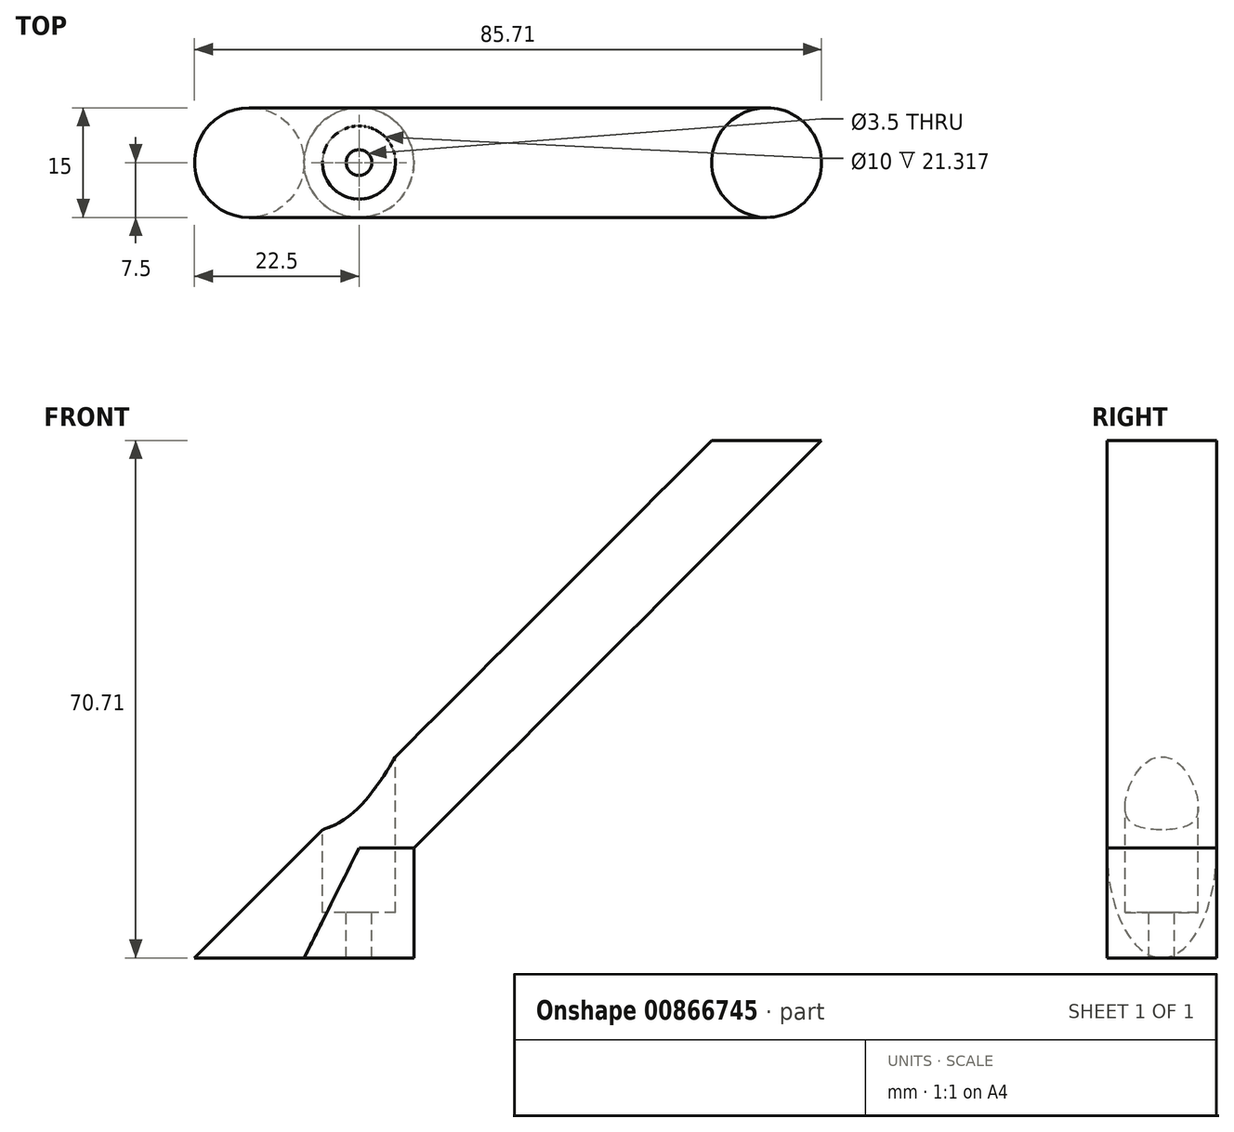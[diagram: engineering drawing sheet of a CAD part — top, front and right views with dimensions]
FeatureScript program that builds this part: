
annotation { "Feature Type Name" : "Feature", "Feature Type Description" : "" }
export const myFeature = defineFeature(function(context is Context, id is Id, definition is map)
    precondition{}
    {
        {
            assignVariable(context, id + "F0", {"variableType" : VariableType.LENGTH, "name" : "InsertWidth", "lengthValue" : 3.5 * mm});
        }
        {
            assignVariable(context, id + "F1", {"variableType" : VariableType.LENGTH, "name" : "LegBaseDepth", "lengthValue" : 15 * mm});
        }
        {
            var Q0;
            Q0=qCreatedBy(makeId("Top.planeOp"),FACE);
            var sketch = newSketch(context, id + "F2", { "sketchPlane" : qUnion([Q0])});
            skCircle(sketch, "E0", {"center": v(0, 0) * mm, "radius": 7.5 * mm});
            skCircle(sketch, "E1", {"center": v(0, 0) * mm, "radius": 1.75 * mm});
            skSolve(sketch);
        }
        {
            var Q0;
            Q0 = qSketchRegion(id + "F2", true);
            var Q1;
            Q1=makeQuery(id+"F2.imprint","IMPRINT",FACE,{"disambiguationData":[TD([[makeQuery(id+"F2.imprint","IMPRINT",EDGE,{"derivedFrom":sQuery(id+"F2.wireOp",EDGE,"E1")}),1.0]])]});
            extrude(context, id + "F3", {"entities" : qUnion([Q0, Q1]), "depth" : getVariable(context, 'LegBaseDepth'), "offsetDistance" : 25 * mm});
        }
        {
            var Q0;
            Q0=qCreatedBy(makeId("Front.planeOp"),FACE);
            var sketch = newSketch(context, id + "F4", { "sketchPlane" : qUnion([Q0])});
            skLineSegment(sketch, "E2", {"start": v(0, 0) * mm, "end": v(70.71, 70.71) * mm});
            skLineSegment(sketch, "E3", {"start": v(0, 0) * mm, "end": v(14.86, 0) * mm});
            skLineSegment(sketch, "E4", {"start": v(70.71, 70.71) * mm, "end": v(65.4, 76.01) * mm});
            skLineSegment(sketch, "E5", {"start": v(70.71, 70.71) * mm, "end": v(76.01, 65.4) * mm});
            skSolve(sketch);
        }
        {
            var Q0;
            Q0=makeQuery(id+"F3.opExtrude","CAP_FACE",FACE,{"disambiguationData":[OSD([sQuery(id+"F2.wireOp",EDGE,"E0")])],"isStart":false});
            var sketch = newSketch(context, id + "F5", { "sketchPlane" : qUnion([Q0])});
            skPoint(sketch, "E6", {"position": v(0, 0) * mm});
            skSolve(sketch);
        }
        {
            var Q0;
            Q0=makeQuery(id+"F5.imprint","IMPRINT",FACE,{"disambiguationData":[TD([[makeQuery(id+"F5.imprint","IMPRINT",EDGE,{"derivedFrom":makeQuery(id+"F3.opExtrude","CAP_EDGE",EDGE,{"disambiguationData":[OSD([sQuery(id+"F2.wireOp",EDGE,"E0")])],"isStart":false})}),1.0]])]});
            var Q1;
            Q1=sQuery(id+"F4.wireOp",EDGE,"E2");
            sweep(context, id + "F6", {"operationType" : NewBodyOperationType.ADD, "profiles" : qUnion([Q0]), "path" : qUnion([Q1])});
        }
        {
            var Q0;
            Q0=qCreatedBy(makeId("Right.planeOp"),FACE);
            var sketch = newSketch(context, id + "F7", { "sketchPlane" : qUnion([Q0])});
            skLineSegment(sketch, "E7", {"start": v(0, 0) * mm, "end": v(0, 43) * mm});
            skPoint(sketch, "E8", {"position": v(0, 17.18) * mm});
            skLineSegment(sketch, "E9", {"start": v(0, 17.18) * mm, "end": v(0, 0) * mm});
            skSolve(sketch);
        }
        {
            var Q0;
            Q0=qCreatedBy(makeId("Top.planeOp"),FACE);
            var Q1;
            Q1=sQuery(id+"F7.wireOp",VERTEX,"E8");
            cPlane(context, id + "F8", {"entities" : qUnion([Q0, Q1]), "cplaneType" : CPlaneType.PLANE_POINT, "offset" : 25 * mm, "width" : 150 * mm, "height" : 150 * mm});
        }
        {
            var Q0;
            Q0=qCreatedBy(id+"F8.planeOp",FACE);
            var sketch = newSketch(context, id + "F9", { "sketchPlane" : qUnion([Q0])});
            skCircle(sketch, "E10", {"center": v(0, 0) * mm, "radius": 1.75 * mm});
            skCircle(sketch, "E11", {"center": v(0, 0) * mm, "radius": 5 * mm});
            skSolve(sketch);
        }
        {
            var Q0;
            Q0=sQuery(id+"F9.wireOp",VERTEX,"E10.center");
            var Q1;
            Q1=makeQuery(id+"F3.opExtrude","SWEPT_BODY",BODY,{"disambiguationData":[OSD([sQuery(id+"F2.wireOp",EDGE,"E0")])]});
            hole(context, id + "F10", {"style" : HoleStyle.C_BORE, "endStyle" : HoleEndStyle.THROUGH, "holeDiameter" : getVariable(context, 'InsertWidth'), "cBoreDiameter" : 10 * mm, "cBoreDepth" : 11 * mm, "majorDiameter" : 5 * mm, "isTappedThrough" : true, "tappedDepth" : 12 * mm, "tapClearance" : 3, "startFromSketch" : true, "locations" : qUnion([Q0]), "scope" : qUnion([Q1])});
        }
        {
            var Q0;
            Q0=makeQuery(id+"F9.imprint","IMPRINT",FACE,{"disambiguationData":[TD([[makeQuery(id+"F9.imprint","IMPRINT",EDGE,{"derivedFrom":sQuery(id+"F9.wireOp",EDGE,"E10")}),-1.0]])]});
            var Q1;
            Q1=makeQuery(id+"F9.imprint","IMPRINT",FACE,{"disambiguationData":[TD([[makeQuery(id+"F9.imprint","IMPRINT",EDGE,{"derivedFrom":sQuery(id+"F9.wireOp",EDGE,"E10")}),1.0]])]});
            extrude(context, id + "F11", {"entities" : qUnion([Q0, Q1]), "operationType" : NewBodyOperationType.REMOVE, "depth" : 25 * mm, "offsetDistance" : 25 * mm});
        }
    });
